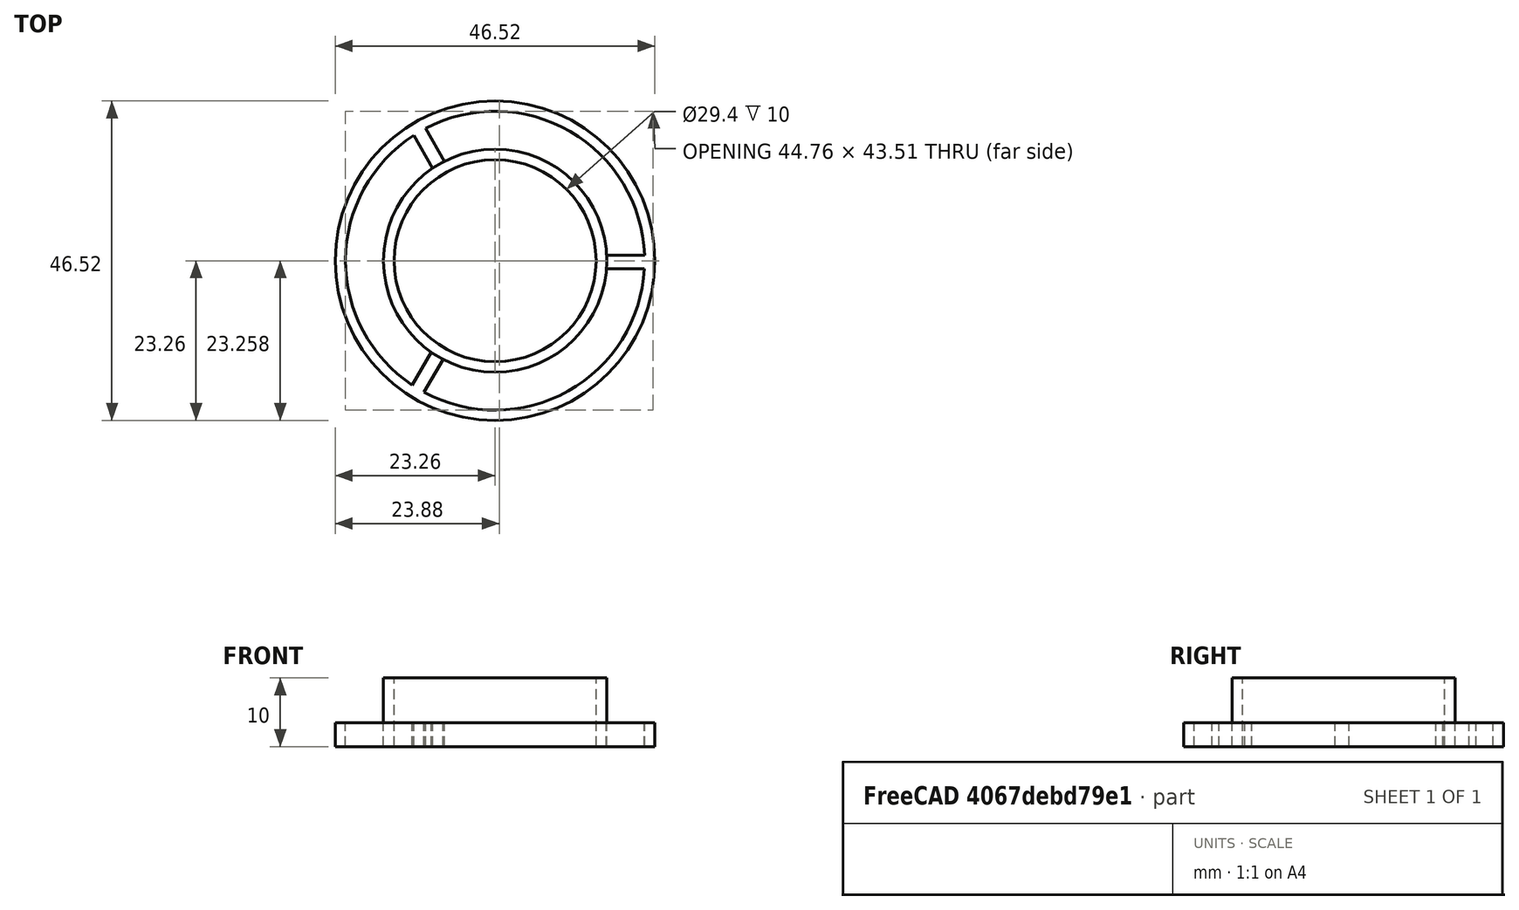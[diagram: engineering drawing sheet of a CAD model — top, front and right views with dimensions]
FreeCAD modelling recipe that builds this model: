
FCSTD DOCUMENT  (FreeCAD 0.16R6712 (Git))
Label: in-out-ring
License: All rights reserved
LicenseURL: http://en.wikipedia.org/wiki/All_rights_reserved
objects: Part::FeaturePython×6, Part::Cylinder×4, Part::Box×3
note: 13 computed .brp shape members not serialized (recipe doc carries the construction recipe); baked Part::Feature solids carry a one-line shape summary decoded from their .brp

FEATURE [Part::Cylinder] Cylinder  label="圆柱体"
  Angle = 360
  Height = 3.5
  Radius = 23.26
FEATURE [Part::Box] Box010  label="立方体007"
  Height = 3.5
  Length = 23
  Placement = pos=(0,-1.2,-32) rot=(0,0,1;0rad)
  Width = 2
FEATURE [Part::Box] Box011  label="立方体008"
  Height = 3.5
  Length = 23
  Placement = pos=(1,0,-32) rot=(0,0,1;2.0944rad)
  Width = 2
FEATURE [Part::Box] Box012  label="立方体009"
  Height = 3.5
  Length = 23
  Placement = pos=(-1,1,-32) rot=(0,0,-1;2.0944rad)
  Width = 2
FEATURE [Part::FeaturePython] Connect  # WARN: FeaturePython — macro-defined, semantics opaque (R4)
  Base = -> Box010
  Mode = 1
  Tool = -> Box011
FEATURE [Part::FeaturePython] Connect001  # WARN: FeaturePython — macro-defined, semantics opaque (R4)
  Base = -> Connect
  Mode = 1
  Placement = pos=(0,0,32) rot=(0,0,1;0rad)
  Tool = -> Box012
FEATURE [Part::Cylinder] Cylinder001  label="圆柱体001"
  Angle = 360
  Height = 7
  Placement = pos=(0,0,-3) rot=(0,0,1;0rad)
  Radius = 21.76
FEATURE [Part::FeaturePython] Cutout  # WARN: FeaturePython — macro-defined, semantics opaque (R4)
  Base = -> Cylinder
  Mode = 3
  Tool = -> Cylinder001
FEATURE [Part::Cylinder] Cylinder002  label="圆柱体002"
  Angle = 360
  Height = 10
  Radius = 16.24
FEATURE [Part::Cylinder] Cylinder003  label="圆柱体003"
  Angle = 360
  Height = 10
  Radius = 14.7
FEATURE [Part::FeaturePython] Connect002  # WARN: FeaturePython — macro-defined, semantics opaque (R4)
  Base = -> Connect001
  Mode = 1
  Tool = -> Cutout
FEATURE [Part::FeaturePython] Connect003  # WARN: FeaturePython — macro-defined, semantics opaque (R4)
  Base = -> Connect002
  Mode = 1
  Tool = -> Cylinder002
FEATURE [Part::FeaturePython] Cutout001  # WARN: FeaturePython — macro-defined, semantics opaque (R4)
  Base = -> Connect003
  Mode = 3
  Tool = -> Cylinder003
